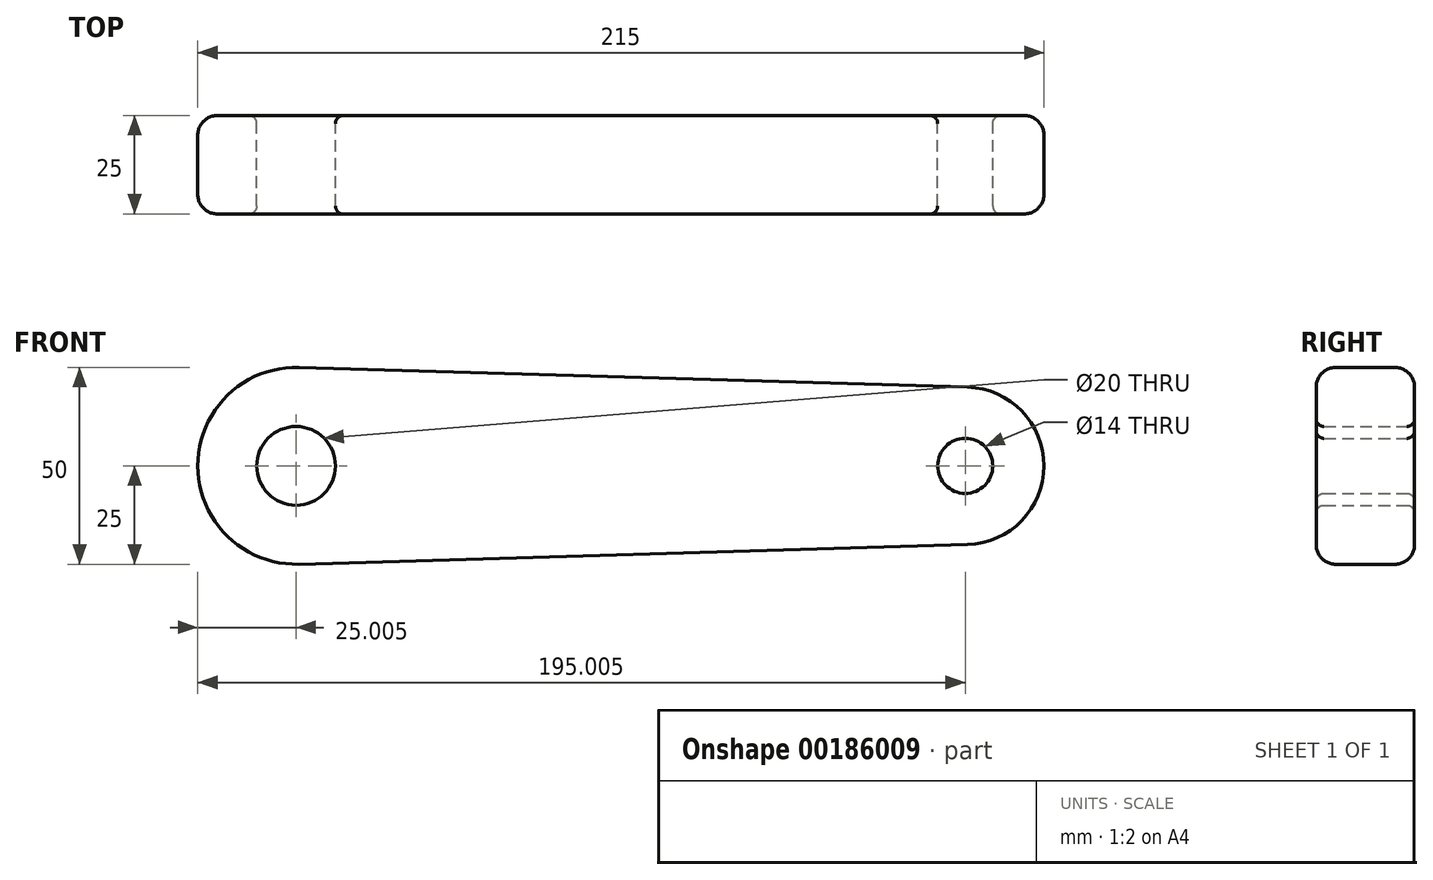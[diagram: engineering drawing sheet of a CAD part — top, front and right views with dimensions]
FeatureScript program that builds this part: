
annotation { "Feature Type Name" : "Feature", "Feature Type Description" : "" }
export const myFeature = defineFeature(function(context is Context, id is Id, definition is map)
    precondition{}
    {
        {
            var Q0;
            Q0=qCreatedBy(makeId("Front.planeOp"),FACE);
            var sketch = newSketch(context, id + "F0", { "sketchPlane" : qUnion([Q0])});
            skCircle(sketch, "E0", {"center": v(-51.98, 0) * mm, "radius": 10 * mm});
            skArc(sketch, "E1", {"start": v(-51.24, 24.99) * mm, "mid": v(-76.98, 0) * mm, "end": v(-51.24, -24.99) * mm});
            skCircle(sketch, "E2", {"center": v(118.02, 0) * mm, "radius": 7 * mm});
            skArc(sketch, "E3", {"start": v(118.61, -20) * mm, "mid": v(138.02, 0) * mm, "end": v(118.61, 20) * mm});
            skLineSegment(sketch, "E4", {"start": v(-51.24, 24.99) * mm, "end": v(118.61, 20) * mm});
            skLineSegment(sketch, "E5", {"start": v(-51.24, -24.99) * mm, "end": v(118.61, -20) * mm});
            skSolve(sketch);
        }
        {
            var Q0;
            Q0=makeQuery(id+"F0.imprint","IMPRINT",FACE,{"disambiguationData":[TD([[makeQuery(id+"F0.imprint","IMPRINT",EDGE,{"derivedFrom":sQuery(id+"F0.wireOp",EDGE,"E0")}),-1.0]])]});
            extrude(context, id + "F1", {"entities" : qUnion([Q0]), "endBound" : BoundingType.SYMMETRIC, "depth" : 25 * mm});
        }
        {
            var Q0;
            Q0=makeQuery(id+"F1.opExtrude","CAP_EDGE",EDGE,{"disambiguationData":[OSD([sQuery(id+"F0.wireOp",EDGE,"E5")])],"isStart":false});
            var Q1;
            Q1=makeQuery(id+"F1.opExtrude","CAP_EDGE",EDGE,{"disambiguationData":[OSD([sQuery(id+"F0.wireOp",EDGE,"E4")])],"isStart":false});
            var Q2;
            Q2=makeQuery(id+"F1.opExtrude","CAP_EDGE",EDGE,{"disambiguationData":[OSD([sQuery(id+"F0.wireOp",EDGE,"E5")])],"isStart":true});
            var Q3;
            Q3=makeQuery(id+"F1.opExtrude","CAP_EDGE",EDGE,{"disambiguationData":[OSD([sQuery(id+"F0.wireOp",EDGE,"E1")])],"isStart":true});
            fillet(context, id + "F2", {"entities" : qUnion([Q0, Q1, Q2, Q3]), "radius" : 5 * mm, "tangentPropagation" : true, "allowEdgeOverflow" : false});
        }
        {
            var Q0;
            Q0=makeQuery(id+"F1.opExtrude","CAP_EDGE",EDGE,{"disambiguationData":[OSD([sQuery(id+"F0.wireOp",EDGE,"E0")])],"isStart":false});
            var Q1;
            Q1=makeQuery(id+"F1.opExtrude","CAP_EDGE",EDGE,{"disambiguationData":[OSD([sQuery(id+"F0.wireOp",EDGE,"E0")])],"isStart":true});
            var Q2;
            Q2=makeQuery(id+"F1.opExtrude","CAP_EDGE",EDGE,{"disambiguationData":[OSD([sQuery(id+"F0.wireOp",EDGE,"E2")])],"isStart":false});
            var Q3;
            Q3=makeQuery(id+"F1.opExtrude","SWEPT_FACE",FACE,{"disambiguationData":[OSD([sQuery(id+"F0.wireOp",EDGE,"E2")])]});
            fillet(context, id + "F3", {"entities" : qUnion([Q0, Q1, Q2, Q3]), "radius" : 2 * mm, "tangentPropagation" : true, "allowEdgeOverflow" : false});
        }
    });
